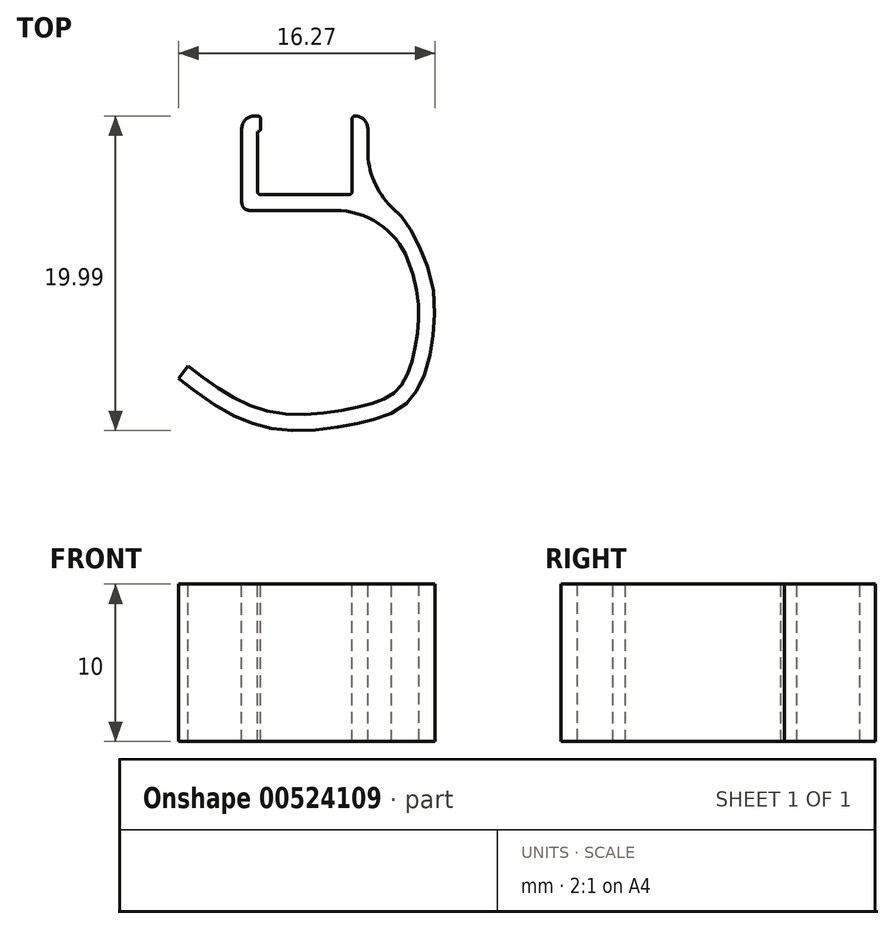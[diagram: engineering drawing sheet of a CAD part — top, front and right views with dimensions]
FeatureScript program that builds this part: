
annotation { "Feature Type Name" : "Feature", "Feature Type Description" : "" }
export const myFeature = defineFeature(function(context is Context, id is Id, definition is map)
    precondition{}
    {
        {
            var Q0;
            Q0=qCreatedBy(makeId("Top.planeOp"),FACE);
            var sketch = newSketch(context, id + "F0", { "sketchPlane" : qUnion([Q0])});
            skLineSegment(sketch, "E0.bottom", {"start": v(0, 0) * mm, "end": v(1, 0) * mm});
            skLineSegment(sketch, "E0.top", {"start": v(0.2, 5) * mm, "end": v(0.2, 5) * mm});
            skLineSegment(sketch, "E0.left", {"start": v(0, 0.8) * mm, "end": v(0, 4.8) * mm});
            skLineSegment(sketch, "E0.right", {"start": v(1, 2.8) * mm, "end": v(1, 4.2) * mm});
            skLineSegment(sketch, "E1", {"start": v(1, 0) * mm, "end": v(1, -1) * mm});
            skLineSegment(sketch, "E2", {"start": v(-2.4, -1) * mm, "end": v(-6.5, -1) * mm});
            skLineSegment(sketch, "E3", {"start": v(-7, -0.5) * mm, "end": v(-7, 4.2) * mm});
            skPoint(sketch, "E4.end.orphan", {"position": v(-7.5, -1) * mm});
            skLineSegment(sketch, "E5", {"start": v(-6.2, 5) * mm, "end": v(-6, 5) * mm});
            skLineSegment(sketch, "E6", {"start": v(-6, 5) * mm, "end": v(-6, 0.2) * mm});
            skLineSegment(sketch, "E7", {"start": v(-5.8, 0) * mm, "end": v(-0.8, 0) * mm});
            skLineSegment(sketch, "E8", {"start": v(-6, 5) * mm, "end": v(-6, 5) * mm});
            skLineSegment(sketch, "E9", {"start": v(-5.8, 4.8) * mm, "end": v(-5.8, 4.2) * mm});
            skLineSegment(sketch, "E10", {"start": v(-6, 4) * mm, "end": v(-6, 4) * mm});
            skPoint(sketch, "E11.end.orphan", {"position": v(-4, -6.31) * mm});
            skPoint(sketch, "E12.end.orphan", {"position": v(-4, -9) * mm});
            skPoint(sketch, "E13.1.internal.orphan", {"position": v(0, -7.41) * mm});
            skPoint(sketch, "E14.visualSharp", {"position": v(1, -1) * mm});
            skPoint(sketch, "E15.visualSharp", {"position": v(1, 0) * mm});
            skLineSegment(sketch, "E16", {"start": v(1.58, -0.18) * mm, "end": v(1.56, -0.17) * mm});
            skPoint(sketch, "E17.visualSharp", {"position": v(-12.35, -11.59) * mm});
            skLineSegment(sketch, "E17.filletArc", {"start": v(-12.35, -11.59) * mm, "end": v(-12.35, -11.59) * mm});
            skPoint(sketch, "E18.visualSharp", {"position": v(-12.68, -16.19) * mm});
            skLineSegment(sketch, "E18.filletArc", {"start": v(-12.68, -16.19) * mm, "end": v(-12.68, -16.19) * mm});
            skPoint(sketch, "E19.3.internal.orphan", {"position": v(0, -14) * mm});
            skLineSegment(sketch, "E20", {"start": v(-2.4, -1) * mm, "end": v(-1.1, -1) * mm});
            skLineSegment(sketch, "E21", {"start": v(1, 0.73) * mm, "end": v(1, 0) * mm});
            skFitSpline(sketch, "E22", {"points": [v(1, -1) * mm, v(2.34, -2.02) * mm, v(4.02, -5.61) * mm, v(4.06, -9.4) * mm, v(3, -12.28) * mm, v(0.57, -13.45) * mm, v(-5.27, -13.78) * mm, v(-10.4, -10.88) * mm], "startDerivative": vector(13.9, -7.77) * mm, "endDerivative": vector(-26.54, 20.51) * mm});
            skFitSpline(sketch, "E23.0", {"points": [v(1.49, -0.13) * mm, v(1.63, -0.2) * mm, v(1.95, -0.39) * mm, v(2.4, -0.7) * mm, v(2.78, -1.02) * mm, v(3.06, -1.31) * mm, v(3.32, -1.64) * mm, v(3.66, -2.12) * mm, v(4.04, -2.79) * mm, v(4.45, -3.67) * mm, v(4.8, -4.6) * mm, v(5.14, -5.9) * mm, v(5.25, -7.14) * mm, v(5.21, -8.33) * mm, v(5.11, -9.2) * mm, v(4.97, -10.04) * mm, v(4.77, -10.9) * mm, v(4.49, -11.73) * mm, v(4.16, -12.39) * mm, v(3.82, -12.87) * mm, v(3.4, -13.31) * mm, v(2.82, -13.74) * mm, v(2.05, -14.08) * mm, v(1.37, -14.28) * mm, v(0.8, -14.42) * mm, v(0.2, -14.56) * mm, v(-0.64, -14.73) * mm, v(-1.72, -14.89) * mm, v(-2.87, -14.98) * mm, v(-4.04, -14.97) * mm, v(-5.02, -14.86) * mm, v(-5.79, -14.69) * mm, v(-6.53, -14.46) * mm, v(-7.4, -14.1) * mm, v(-8.39, -13.56) * mm, v(-9.6, -12.76) * mm, v(-10.46, -12.1) * mm, v(-11, -11.68) * mm]});
            skLineSegment(sketch, "E24", {"start": v(-11, -11.68) * mm, "end": v(-10.4, -10.88) * mm});
            skArc(sketch, "E25.filletArc", {"start": v(3.54, -4.12) * mm, "mid": v(1.7, -1.85) * mm, "end": v(-1.1, -1) * mm});
            skArc(sketch, "E26.filletArc", {"start": v(1, 2.8) * mm, "mid": v(1.43, 0.76) * mm, "end": v(2.66, -0.92) * mm});
            skPoint(sketch, "E27.visualSharp", {"position": v(1, 5) * mm});
            skArc(sketch, "E27.filletArc", {"start": v(1, 4.2) * mm, "mid": v(0.77, 4.77) * mm, "end": v(0.2, 5) * mm});
            skPoint(sketch, "E28.visualSharp", {"position": v(0, 0) * mm});
            skPoint(sketch, "E29.visualSharp", {"position": v(-6, 0) * mm});
            skArc(sketch, "E29.filletArc", {"start": v(-6, 0.2) * mm, "mid": v(-5.94, 0.06) * mm, "end": v(-5.8, 0) * mm});
            skLineSegment(sketch, "E30", {"start": v(-0.8, 0) * mm, "end": v(-0.2, 0) * mm});
            skLineSegment(sketch, "E31", {"start": v(0, 0.8) * mm, "end": v(0, 0.2) * mm});
            skArc(sketch, "E32.filletArc", {"start": v(-0.2, 0) * mm, "mid": v(-0.06, 0.06) * mm, "end": v(0, 0.2) * mm});
            skPoint(sketch, "E33.visualSharp", {"position": v(-7, -1) * mm});
            skArc(sketch, "E33.filletArc", {"start": v(-7, -0.5) * mm, "mid": v(-6.85, -0.85) * mm, "end": v(-6.5, -1) * mm});
            skPoint(sketch, "E34.visualSharp", {"position": v(-7, 5) * mm});
            skArc(sketch, "E34.filletArc", {"start": v(-6.2, 5) * mm, "mid": v(-6.77, 4.77) * mm, "end": v(-7, 4.2) * mm});
            skPoint(sketch, "E35.visualSharp", {"position": v(0, 5) * mm});
            skArc(sketch, "E35.filletArc", {"start": v(0.2, 5) * mm, "mid": v(0.06, 4.94) * mm, "end": v(0, 4.8) * mm});
            skPoint(sketch, "E36.visualSharp", {"position": v(-5.8, 5) * mm});
            skArc(sketch, "E36.filletArc", {"start": v(-5.8, 4.8) * mm, "mid": v(-5.86, 4.94) * mm, "end": v(-6, 5) * mm});
            skPoint(sketch, "E37.visualSharp", {"position": v(-5.8, 4) * mm});
            skArc(sketch, "E37.filletArc", {"start": v(-6, 4) * mm, "mid": v(-5.86, 4.06) * mm, "end": v(-5.8, 4.2) * mm});
            skSolve(sketch);
        }
        {
            var Q0;
            Q0=makeQuery(id+"F0.imprint","IMPRINT",FACE,{"disambiguationData":[TD([[makeQuery(id+"F0.imprint","IMPRINT",EDGE,{"derivedFrom":sQuery(id+"F0.wireOp",EDGE,"E0.left")}),-1.0]])]});
            var Q1;
            Q1=makeQuery(id+"F0.imprint","IMPRINT",FACE,{"disambiguationData":[TD([[makeQuery(id+"F0.imprint","IMPRINT",EDGE,{"derivedFrom":sQuery(id+"F0.wireOp",EDGE,"E9")}),-1.0]])]});
            extrude(context, id + "F1", {"entities" : qUnion([Q0, Q1]), "oppositeDirection" : true, "depth" : 10 * mm, "offsetDistance" : 25 * mm});
        }
    });
